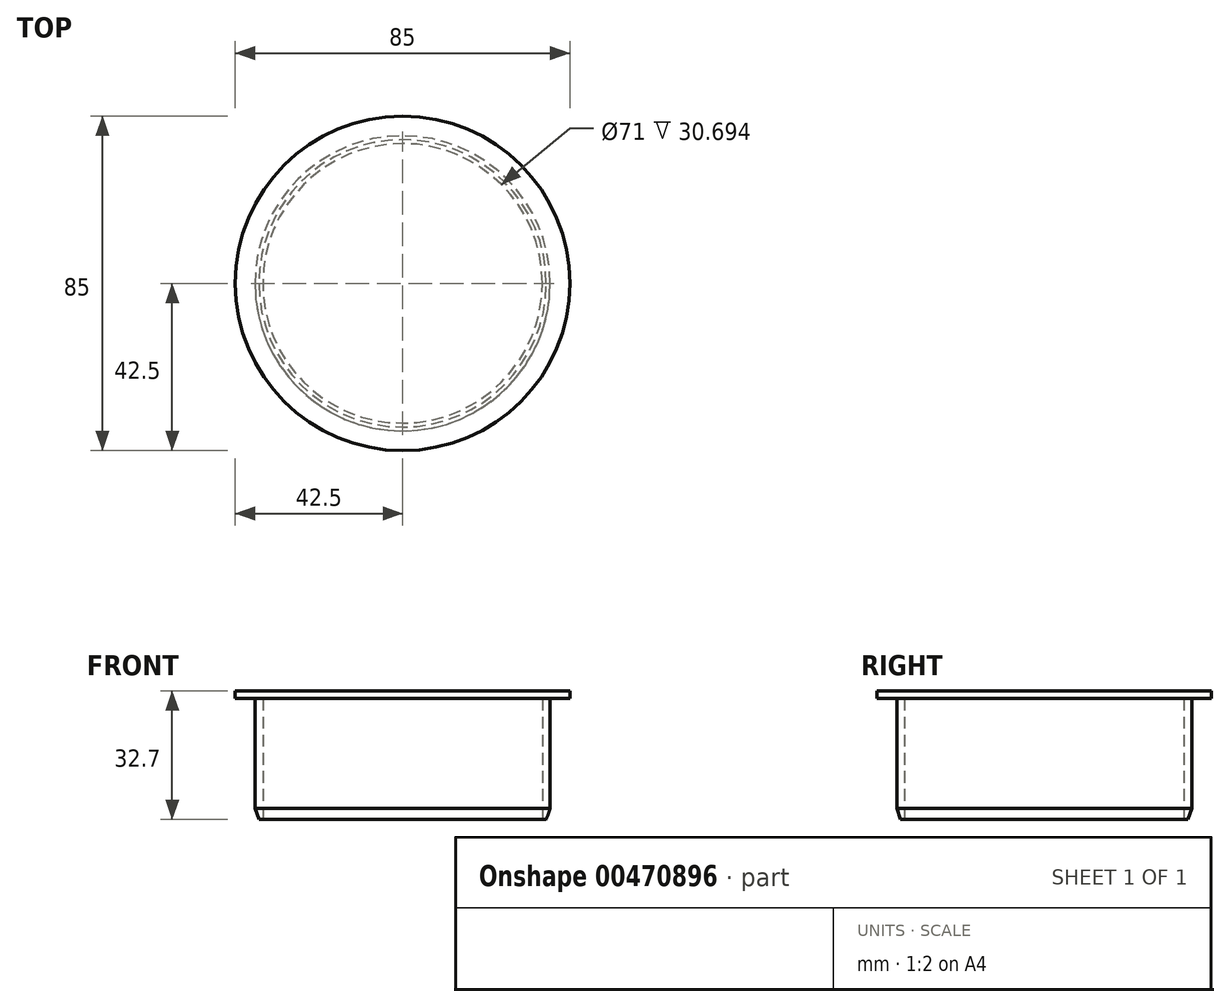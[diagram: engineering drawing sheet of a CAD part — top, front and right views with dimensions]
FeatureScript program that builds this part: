
annotation { "Feature Type Name" : "Feature", "Feature Type Description" : "" }
export const myFeature = defineFeature(function(context is Context, id is Id, definition is map)
    precondition{}
    {
        {
            var Q0;
            Q0=qCreatedBy(makeId("Front.planeOp"),FACE);
            var sketch = newSketch(context, id + "F0", { "sketchPlane" : qUnion([Q0])});
            skLineSegment(sketch, "E0", {"start": v(0, 45.9) * mm, "end": v(-42.5, 45.9) * mm});
            skLineSegment(sketch, "E1", {"start": v(-42.5, 45.9) * mm, "end": v(-42.5, 43.9) * mm});
            skLineSegment(sketch, "E2", {"start": v(-42.5, 43.9) * mm, "end": v(-37.5, 43.9) * mm});
            skLineSegment(sketch, "E3", {"start": v(-37.5, 43.9) * mm, "end": v(-37.5, 13.2) * mm});
            skLineSegment(sketch, "E4", {"start": v(-37.5, 13.2) * mm, "end": v(-35.5, 13.2) * mm});
            skLineSegment(sketch, "E5", {"start": v(-35.5, 13.2) * mm, "end": v(-35.5, 43.9) * mm});
            skLineSegment(sketch, "E6", {"start": v(-35.5, 43.9) * mm, "end": v(0, 43.9) * mm});
            skLineSegment(sketch, "E7", {"start": v(0, 43.9) * mm, "end": v(0, 45.9) * mm});
            skLineSegment(sketch, "E8", {"start": v(0, -27.29) * mm, "end": v(0, 68.17) * mm, "construction": true});
            skSolve(sketch);
        }
        {
            var Q0;
            Q0 = qSketchRegion(id + "F0", true);
            var Q1;
            Q1=sQuery(id+"F0.wireOp",EDGE,"E8");
            revolve(context, id + "F1", {"entities" : qUnion([Q0]), "axis" : qUnion([Q1]), "revolveType" : RevolveType.FULL});
        }
        {
            var Q0;
            Q0=makeQuery(id+"F1.opRevolve","SWEPT_EDGE",EDGE,{"disambiguationData":[OSD([sQuery(id+"F0.wireOp",EDGE,"E3"),sQuery(id+"F0.wireOp",EDGE,"E4")])]});
            chamfer(context, id + "F2", {"entities" : qUnion([Q0]), "chamferType" : ChamferType.OFFSET_ANGLE, "width" : 1 * mm, "oppositeDirection" : false, "angle" : 70 * degree, "tangentPropagation" : true});
        }
    });
